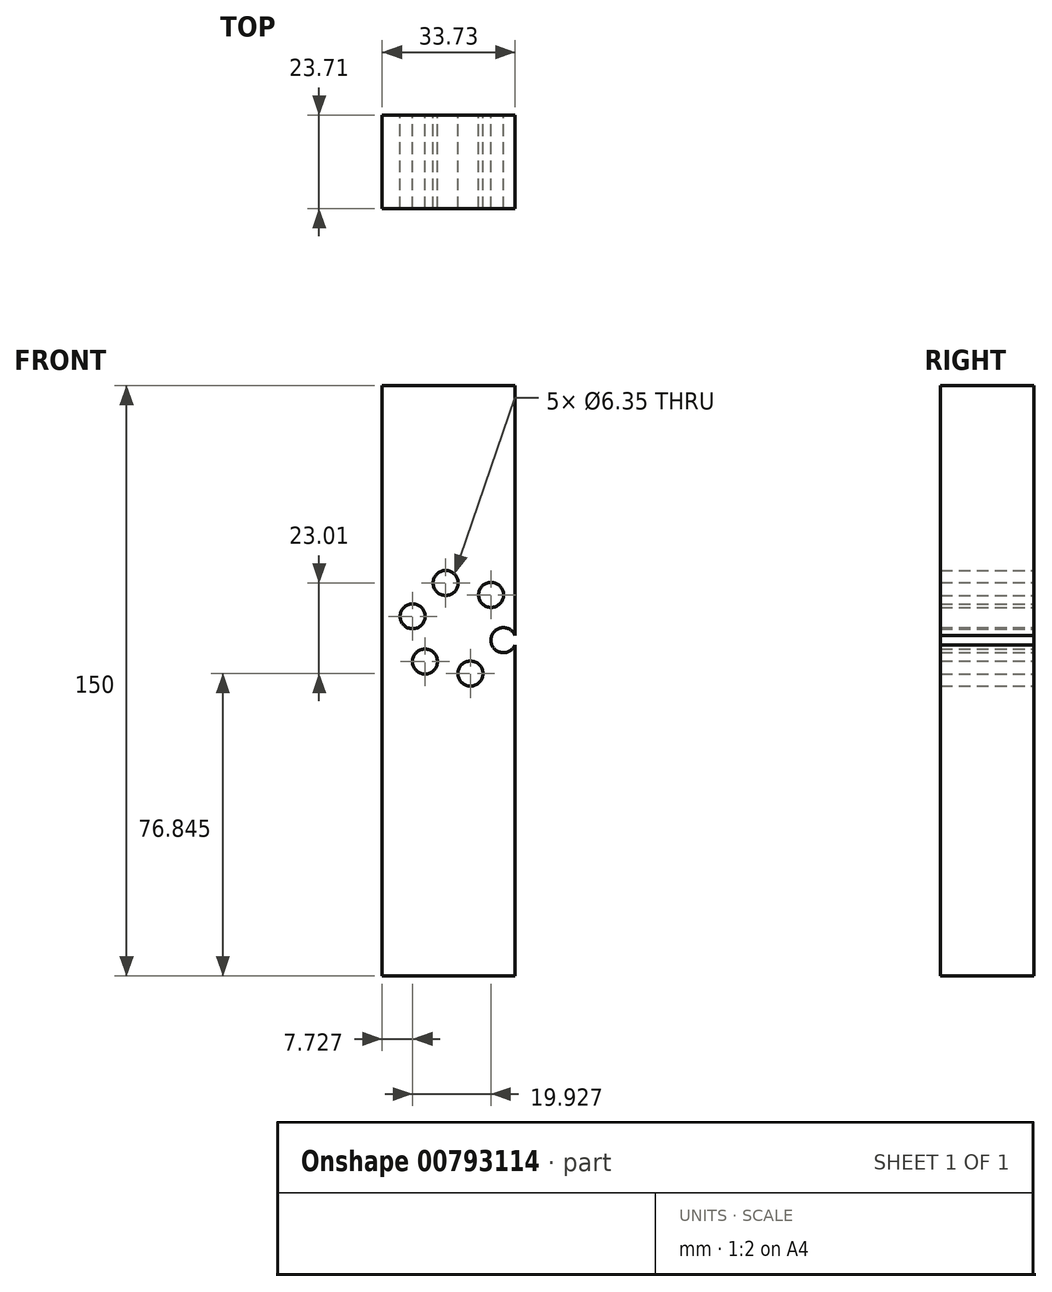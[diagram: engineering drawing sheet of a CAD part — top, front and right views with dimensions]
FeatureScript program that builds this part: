
annotation { "Feature Type Name" : "Feature", "Feature Type Description" : "" }
export const myFeature = defineFeature(function(context is Context, id is Id, definition is map)
    precondition{}
    {
        {
            var Q0;
            Q0=qCreatedBy(makeId("Top.planeOp"),FACE);
            var sketch = newSketch(context, id + "F0", { "sketchPlane" : qUnion([Q0])});
            skLineSegment(sketch, "E0.bottom", {"start": v(-33.73, 23.7) * mm, "end": v(0, 23.7) * mm});
            skLineSegment(sketch, "E0.top", {"start": v(-33.73, 0) * mm, "end": v(0, 0) * mm});
            skLineSegment(sketch, "E0.left", {"start": v(-33.73, 23.7) * mm, "end": v(-33.73, 0) * mm});
            skLineSegment(sketch, "E0.right", {"start": v(0, 23.7) * mm, "end": v(0, 0) * mm});
            skSolve(sketch);
        }
        {
            var Q0;
            Q0 = qSketchRegion(id + "F0", true);
            extrude(context, id + "F1", {"entities" : qUnion([Q0]), "endBound" : BoundingType.SYMMETRIC, "depth" : 150 * mm, "offsetDistance" : 25.4 * mm});
        }
        {
            var Q0;
            Q0=makeQuery(id+"F1.opExtrude","SWEPT_FACE",FACE,{"disambiguationData":[OSD([sQuery(id+"F0.wireOp",EDGE,"E0.bottom")])]});
            var sketch = newSketch(context, id + "F2", { "sketchPlane" : qUnion([Q0])});
            skCircle(sketch, "E1.cCircle", {"center": v(14.47, 13.35) * mm, "radius": 11.93 * mm, "construction": true});
            skLineSegment(sketch, "E1.0", {"start": v(17.61, 24.85) * mm, "end": v(26, 16.38) * mm});
            skLineSegment(sketch, "E1.1", {"start": v(26, 16.38) * mm, "end": v(22.86, 4.88) * mm});
            skLineSegment(sketch, "E1.2", {"start": v(22.86, 4.88) * mm, "end": v(11.33, 1.84) * mm});
            skLineSegment(sketch, "E1.3", {"start": v(11.33, 1.84) * mm, "end": v(2.94, 10.32) * mm});
            skLineSegment(sketch, "E1.4", {"start": v(2.94, 10.32) * mm, "end": v(6.08, 21.82) * mm});
            skLineSegment(sketch, "E1.5", {"start": v(6.08, 21.82) * mm, "end": v(17.61, 24.85) * mm});
            skSolve(sketch);
        }
        {
            var Q0;
            Q0=sQuery(id+"F2.wireOp",VERTEX,"E1.0.start");
            var Q1;
            Q1=sQuery(id+"F2.wireOp",VERTEX,"E1.2.end");
            var Q2;
            Q2=sQuery(id+"F2.wireOp",VERTEX,"E1.2.start");
            var Q3;
            Q3=sQuery(id+"F2.wireOp",VERTEX,"E1.5.start");
            var Q4;
            Q4=sQuery(id+"F2.wireOp",VERTEX,"E1.4.start");
            var Q5;
            Q5=sQuery(id+"F2.wireOp",VERTEX,"E1.1.start");
            var Q6;
            Q6=makeQuery(id+"F1.opExtrude","SWEPT_BODY",BODY,{"disambiguationData":[OSD([sQuery(id+"F0.wireOp",EDGE,"E0.bottom"),sQuery(id+"F0.wireOp",EDGE,"E0.top"),sQuery(id+"F0.wireOp",EDGE,"E0.left"),sQuery(id+"F0.wireOp",EDGE,"E0.right")])]});
            hole(context, id + "F3", {"style" : HoleStyle.SIMPLE, "endStyle" : HoleEndStyle.THROUGH, "holeDiameter" : 6.35 * mm, "majorDiameter" : 6.35 * mm, "isTappedThrough" : true, "tappedDepth" : 12.7 * mm, "tapClearance" : 3, "locations" : qUnion([Q0, Q1, Q2, Q3, Q4, Q5]), "scope" : qUnion([Q6])});
        }
        {
            var Q0;
            Q0=makeQuery(id+"F1.opExtrude","SWEPT_FACE",FACE,{"disambiguationData":[OSD([sQuery(id+"F0.wireOp",EDGE,"E0.bottom")])]});
            var sketch = newSketch(context, id + "F4", { "sketchPlane" : qUnion([Q0])});
            skLineSegment(sketch, "E2", {"start": v(-16.38, 67.95) * mm, "end": v(-16.38, -70.88) * mm});
            skSolve(sketch);
        }
    });
